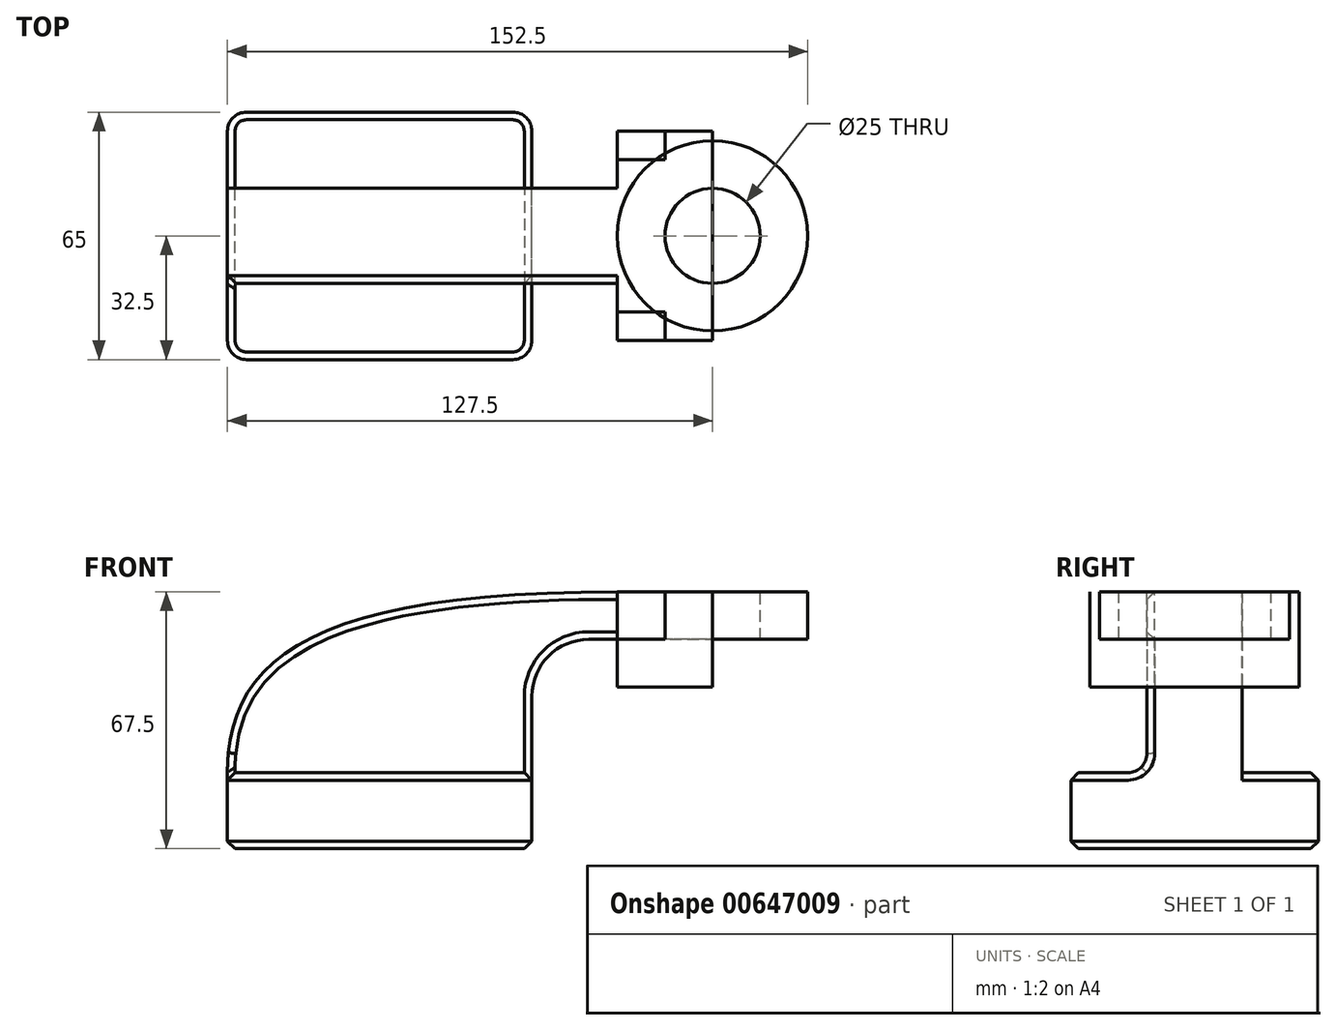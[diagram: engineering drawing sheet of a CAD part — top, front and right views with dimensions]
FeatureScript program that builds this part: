
annotation { "Feature Type Name" : "Feature", "Feature Type Description" : "" }
export const myFeature = defineFeature(function(context is Context, id is Id, definition is map)
    precondition{}
    {
        {
            var Q0;
            Q0=qCreatedBy(makeId("Front.planeOp"),FACE);
            var sketch = newSketch(context, id + "F0", { "sketchPlane" : qUnion([Q0])});
            skLineSegment(sketch, "E0.bottom", {"start": v(40, -10) * mm, "end": v(-40, -10) * mm});
            skLineSegment(sketch, "E0.top", {"start": v(40, 10) * mm, "end": v(-40, 10) * mm});
            skLineSegment(sketch, "E0.left", {"start": v(40, -10) * mm, "end": v(40, 10) * mm});
            skLineSegment(sketch, "E0.right", {"start": v(-40, -10) * mm, "end": v(-40, 10) * mm});
            skPoint(sketch, "E0.middle", {"position": v(0, 0) * mm});
            skLineSegment(sketch, "E1.bottom", {"start": v(62.5, 57.5) * mm, "end": v(87.5, 57.5) * mm});
            skLineSegment(sketch, "E1.top", {"start": v(62.5, 32.5) * mm, "end": v(87.5, 32.5) * mm});
            skLineSegment(sketch, "E1.left", {"start": v(62.5, 57.5) * mm, "end": v(62.5, 32.5) * mm});
            skLineSegment(sketch, "E1.right", {"start": v(87.5, 57.5) * mm, "end": v(87.5, 32.5) * mm});
            skPoint(sketch, "E1.middle", {"position": v(75, 45) * mm});
            skLineSegment(sketch, "E2", {"start": v(40, 10) * mm, "end": v(40, 30) * mm});
            skArc(sketch, "E3", {"start": v(40, 30) * mm, "mid": v(44.4, 40.6) * mm, "end": v(55, 45) * mm});
            skLineSegment(sketch, "E4", {"start": v(55, 45) * mm, "end": v(75, 45) * mm});
            skPoint(sketch, "E4.endSnap0", {"position": v(75, 57.5) * mm});
            skFitSpline(sketch, "E5", {"points": [v(-40, 10) * mm, v(62.5, 57.5) * mm], "startDerivative": vector(0, 90) * mm, "endDerivative": vector(240, 0) * mm});
            skLineSegment(sketch, "E6", {"start": v(75, 57.5) * mm, "end": v(75, 45) * mm});
            skSolve(sketch);
        }
        {
            var Q0;
            Q0=makeQuery(id+"F0.imprint","IMPRINT",FACE,{"disambiguationData":[TD([[makeQuery(id+"F0.imprint","IMPRINT",EDGE,{"derivedFrom":sQuery(id+"F0.wireOp",EDGE,"E0.top")}),-1.0]])]});
            extrude(context, id + "F1", {"entities" : qUnion([Q0]), "endBound" : BoundingType.SYMMETRIC, "depth" : 25 * mm, "offsetDistance" : 25 * mm});
        }
        {
            var Q0;
            Q0=makeQuery(id+"F0.imprint","IMPRINT",FACE,{"disambiguationData":[TD([[makeQuery(id+"F0.imprint","IMPRINT",EDGE,{"derivedFrom":sQuery(id+"F0.wireOp",EDGE,"E0.bottom")}),-1.0]])]});
            extrude(context, id + "F2", {"entities" : qUnion([Q0]), "operationType" : NewBodyOperationType.ADD, "endBound" : BoundingType.SYMMETRIC, "depth" : 65 * mm, "offsetDistance" : 25 * mm});
        }
        {
            var Q0;
            {var subQ3=sQuery(id+"F0.wireOp",EDGE,"E1.bottom");Q0=makeQuery(id+"F0.imprint","IMPRINT",FACE,{"disambiguationData":[TD([[makeQuery(id+"F0.imprint","IMPRINT",EDGE,{"derivedFrom":subQ3}),-1.0]])]});}
            extrude(context, id + "F3", {"entities" : qUnion([Q0]), "operationType" : NewBodyOperationType.ADD, "endBound" : BoundingType.SYMMETRIC, "depth" : 40 * mm, "offsetDistance" : 25 * mm});
        }
        {
            var Q0;
            {var subQ2=sQuery(id+"F0.wireOp",EDGE,"E1.top");Q0=makeQuery(id+"F0.imprint","IMPRINT",FACE,{"disambiguationData":[TD([[makeQuery(id+"F0.imprint","IMPRINT",EDGE,{"derivedFrom":subQ2}),1.0]])]});}
            extrude(context, id + "F4", {"entities" : qUnion([Q0]), "operationType" : NewBodyOperationType.ADD, "endBound" : BoundingType.SYMMETRIC, "depth" : 55 * mm, "offsetDistance" : 25 * mm});
        }
        {
            var Q0;
            {var subQ3=sQuery(id+"F0.wireOp",EDGE,"E6");Q0=makeQuery(id+"F0.imprint","IMPRINT",FACE,{"disambiguationData":[TD([[makeQuery(id+"F0.imprint","IMPRINT",EDGE,{"derivedFrom":subQ3}),-1.0]])]});}
            var Q1;
            Q1=sQuery(id+"F0.wireOp",EDGE,"E6");
            var Q2;
            Q2=sQuery(id+"F0.wireOp",EDGE,"E1.right");
            revolve(context, id + "F5", {"entities" : qUnion([Q0]), "surfaceEntities" : qUnion([Q1]), "axis" : qUnion([Q2]), "revolveType" : RevolveType.FULL});
        }
        {
            var Q0;
            Q0=makeQuery(id+"F1.opExtrude","CAP_EDGE",EDGE,{"disambiguationData":[OSD([sQuery(id+"F0.wireOp",EDGE,"E0.top")])],"isStart":false});
            var Q1;
            Q1=makeQuery(id+"F2.opExtrude","CAP_EDGE",EDGE,{"disambiguationData":[OSD([sQuery(id+"F0.wireOp",EDGE,"E0.left")])],"isStart":false});
            var Q2;
            Q2=makeQuery(id+"F2.opExtrude","CAP_EDGE",EDGE,{"disambiguationData":[OSD([sQuery(id+"F0.wireOp",EDGE,"E0.left")])],"isStart":true});
            var Q3;
            Q3=makeQuery(id+"F2.opExtrude","CAP_EDGE",EDGE,{"disambiguationData":[OSD([sQuery(id+"F0.wireOp",EDGE,"E0.right")])],"isStart":false});
            var Q4;
            Q4=makeQuery(id+"F2.opExtrude","CAP_EDGE",EDGE,{"disambiguationData":[OSD([sQuery(id+"F0.wireOp",EDGE,"E0.right")])],"isStart":true});
            var Q5;
            Q5=makeQuery(id+"F1.opExtrude","CAP_EDGE",EDGE,{"disambiguationData":[OSD([sQuery(id+"F0.wireOp",EDGE,"E0.top")])],"isStart":true});
            fillet(context, id + "F6", {"entities" : qUnion([Q0, Q1, Q2, Q3, Q4, Q5]), "radius" : 5 * mm, "tangentPropagation" : true, "allowEdgeOverflow" : false});
        }
        {
            var Q0;
            Q0=makeQuery(id+"F2.opExtrude","CAP_EDGE",EDGE,{"disambiguationData":[OSD([sQuery(id+"F0.wireOp",EDGE,"E0.top")])],"isStart":true});
            var Q1;
            {var subQ0=sQuery(id+"F0.wireOp",EDGE,"E0.left");var subQ1=sQuery(id+"F0.wireOp",EDGE,"E0.top");var subQ2=sQuery(id+"F0.wireOp",EDGE,"E2");Q1=makeQuery(id+"F2.boolean.opBoolean","SPLIT",EDGE,{"disambiguationData":[TD([makeQuery(id+"F2.opExtrude","CAP_FACE",FACE,{"disambiguationData":[OSD([sQuery(id+"F0.wireOp",EDGE,"E0.bottom"),subQ1,subQ0,sQuery(id+"F0.wireOp",EDGE,"E0.right")])],"isStart":false})])],"derivedFrom":makeQuery(id+"F2.opExtrude","SWEPT_EDGE",EDGE,{"disambiguationData":[OSD([subQ1,subQ0,subQ2])]})});}
            var Q2;
            Q2=makeQuery(id+"F2.opExtrude","CAP_EDGE",EDGE,{"disambiguationData":[OSD([sQuery(id+"F0.wireOp",EDGE,"E0.bottom")])],"isStart":true});
            chamfer(context, id + "F7", {"entities" : qUnion([Q0, Q1, Q2]), "width" : 2 * mm, "tangentPropagation" : true});
        }
    });
